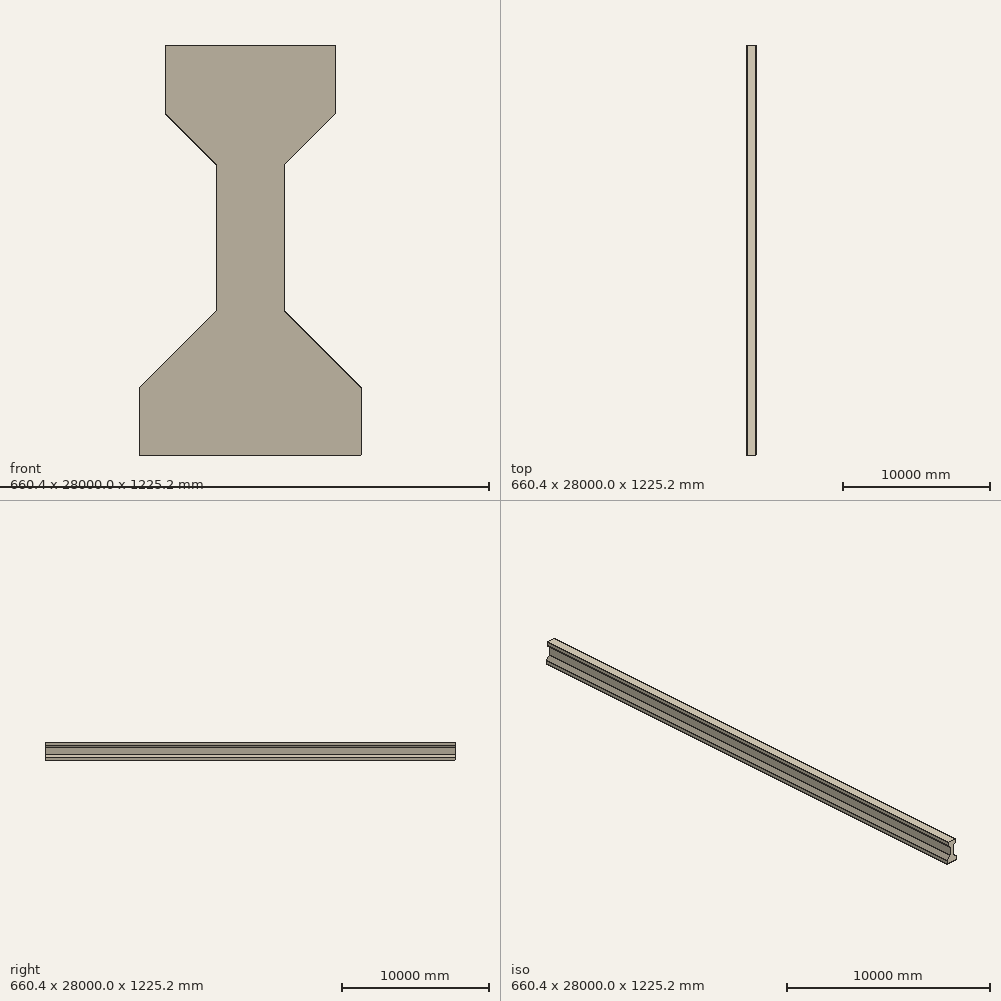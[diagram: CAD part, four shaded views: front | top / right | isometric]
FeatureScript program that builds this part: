
annotation { "Feature Type Name" : "Feature", "Feature Type Description" : "" }
export const myFeature = defineFeature(function(context is Context, id is Id, definition is map)
    precondition{}
    {
        {
            var Q0;
            Q0=qCreatedBy(makeId("Front.planeOp"),FACE);
            var sketch = newSketch(context, id + "F0", { "sketchPlane" : qUnion([Q0])});
            skLineSegment(sketch, "E0", {"start": v(-101.6, 235.65) * mm, "end": v(-101.6, -202.17) * mm});
            skLineSegment(sketch, "E1", {"start": v(-101.6, 235.65) * mm, "end": v(-254, 388.05) * mm});
            skLineSegment(sketch, "E2", {"start": v(-254, 388.05) * mm, "end": v(-254, 591.25) * mm});
            skLineSegment(sketch, "E3", {"start": v(-254, 591.25) * mm, "end": v(0, 591.25) * mm});
            skLineSegment(sketch, "E4", {"start": v(-101.6, -202.17) * mm, "end": v(-330.2, -430.77) * mm});
            skLineSegment(sketch, "E5", {"start": v(-330.2, -430.77) * mm, "end": v(-330.2, -633.97) * mm});
            skLineSegment(sketch, "E6", {"start": v(-330.2, -633.97) * mm, "end": v(0, -633.97) * mm});
            skLineSegment(sketch, "E7.MirrorCS", {"start": v(254, 591.25) * mm, "end": v(0, 591.25) * mm});
            skLineSegment(sketch, "E8.MirrorCS", {"start": v(254, 388.05) * mm, "end": v(254, 591.25) * mm});
            skLineSegment(sketch, "E9.MirrorCS", {"start": v(101.6, 235.65) * mm, "end": v(254, 388.05) * mm});
            skLineSegment(sketch, "E10.MirrorCS", {"start": v(101.6, 235.65) * mm, "end": v(101.6, -202.17) * mm});
            skLineSegment(sketch, "E11.MirrorCS", {"start": v(101.6, -202.17) * mm, "end": v(330.2, -430.77) * mm});
            skLineSegment(sketch, "E12.MirrorCS", {"start": v(330.2, -430.77) * mm, "end": v(330.2, -633.97) * mm});
            skLineSegment(sketch, "E13.MirrorCS", {"start": v(330.2, -633.97) * mm, "end": v(0, -633.97) * mm});
            skSolve(sketch);
        }
        {
            var Q0;
            Q0=makeQuery(id+"F0.imprint","IMPRINT",FACE,{"disambiguationData":[TD([[makeQuery(id+"F0.imprint","IMPRINT",EDGE,{"derivedFrom":sQuery(id+"F0.wireOp",EDGE,"E0")}),1.0]])]});
            extrude(context, id + "F1", {"entities" : qUnion([Q0]), "depth" : 28000 * mm});
        }
    });
